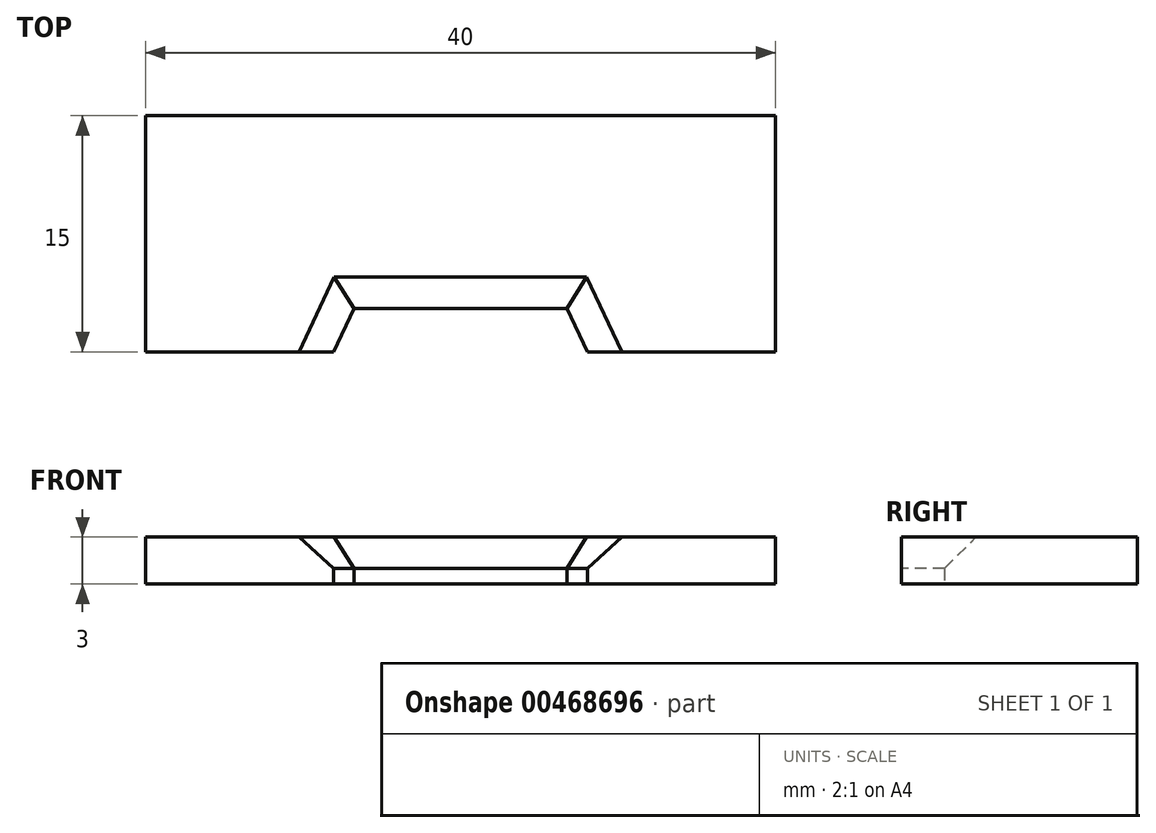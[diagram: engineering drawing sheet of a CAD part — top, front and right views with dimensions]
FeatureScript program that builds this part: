
annotation { "Feature Type Name" : "Feature", "Feature Type Description" : "" }
export const myFeature = defineFeature(function(context is Context, id is Id, definition is map)
    precondition{}
    {
        {
            var Q0;
            Q0=qCreatedBy(makeId("Top.planeOp"),FACE);
            var sketch = newSketch(context, id + "F0", { "sketchPlane" : qUnion([Q0])});
            skLineSegment(sketch, "E0.bottom", {"start": v(20, -7.5) * mm, "end": v(-20, -7.5) * mm});
            skLineSegment(sketch, "E0.top", {"start": v(20, 7.5) * mm, "end": v(-20, 7.5) * mm});
            skLineSegment(sketch, "E0.left", {"start": v(20, -7.5) * mm, "end": v(20, 7.5) * mm});
            skLineSegment(sketch, "E0.right", {"start": v(-20, -7.5) * mm, "end": v(-20, 7.5) * mm});
            skPoint(sketch, "E0.middle", {"position": v(0, 0) * mm});
            skPoint(sketch, "E1", {"position": v(0, -7.5) * mm});
            skLineSegment(sketch, "E2", {"start": v(0, -7.5) * mm, "end": v(-6.75, -7.5) * mm});
            skLineSegment(sketch, "E3", {"start": v(0, -7.5) * mm, "end": v(6.75, -7.5) * mm});
            skLineSegment(sketch, "E4", {"start": v(-6.75, -7.5) * mm, "end": v(-8.05, -7.5) * mm});
            skLineSegment(sketch, "E5", {"start": v(6.75, -7.5) * mm, "end": v(8.05, -7.5) * mm});
            skLineSegment(sketch, "E6", {"start": v(0, -7.5) * mm, "end": v(0, -4.75) * mm});
            skLineSegment(sketch, "E7", {"start": v(0, -4.75) * mm, "end": v(-6.75, -4.75) * mm});
            skLineSegment(sketch, "E8", {"start": v(-6.75, -4.75) * mm, "end": v(-8.05, -7.5) * mm});
            skLineSegment(sketch, "E9", {"start": v(0, -4.75) * mm, "end": v(6.75, -4.75) * mm});
            skLineSegment(sketch, "E10", {"start": v(6.75, -4.75) * mm, "end": v(8.05, -7.5) * mm});
            skSolve(sketch);
        }
        {
            var Q0;
            Q0=makeQuery(id+"F0.imprint","IMPRINT",FACE,{"disambiguationData":[TD([[makeQuery(id+"F0.imprint","IMPRINT",EDGE,{"derivedFrom":sQuery(id+"F0.wireOp",EDGE,"E0.top")}),1.0]])]});
            extrude(context, id + "F1", {"entities" : qUnion([Q0]), "depth" : 3 * mm});
        }
        {
            var Q0;
            Q0=makeQuery(id+"F1.opExtrude","CAP_EDGE",EDGE,{"disambiguationData":[OSD([sQuery(id+"F0.wireOp",EDGE,"gfhMjLmv-TCpJ-DsVg-BH4L-iOuhXFESiVvi")])],"isStart":false});
            var Q1;
            Q1=makeQuery(id+"F1.opExtrude","CAP_EDGE",EDGE,{"disambiguationData":[OSD([sQuery(id+"F0.wireOp",EDGE,"dvy5Beej-kqSq-BQ27-wt73-IXPqbN6oU8sZ")])],"isStart":false});
            var Q2;
            Q2=makeQuery(id+"F1.opExtrude","CAP_EDGE",EDGE,{"disambiguationData":[OSD([sQuery(id+"F0.wireOp",EDGE,"ahkot3L2-g6K3-HbmJ-Qz8h-1ZdLyd6l0aTR")])],"isStart":false});
            var Q3;
            Q3=makeQuery(id+"F1.opExtrude","CAP_EDGE",EDGE,{"disambiguationData":[OSD([sQuery(id+"F0.wireOp",EDGE,"E8")])],"isStart":false});
            var Q4;
            Q4=makeQuery(id+"F1.opExtrude","CAP_EDGE",EDGE,{"disambiguationData":[OSD([sQuery(id+"F0.wireOp",EDGE,"E7"),sQuery(id+"F0.wireOp",EDGE,"E9")])],"isStart":false});
            var Q5;
            Q5=makeQuery(id+"F1.opExtrude","CAP_EDGE",EDGE,{"disambiguationData":[OSD([sQuery(id+"F0.wireOp",EDGE,"E10")])],"isStart":false});
            chamfer(context, id + "F2", {"entities" : qUnion([Q0, Q1, Q2, Q3, Q4, Q5]), "width" : 2 * mm, "tangentPropagation" : true});
        }
    });
